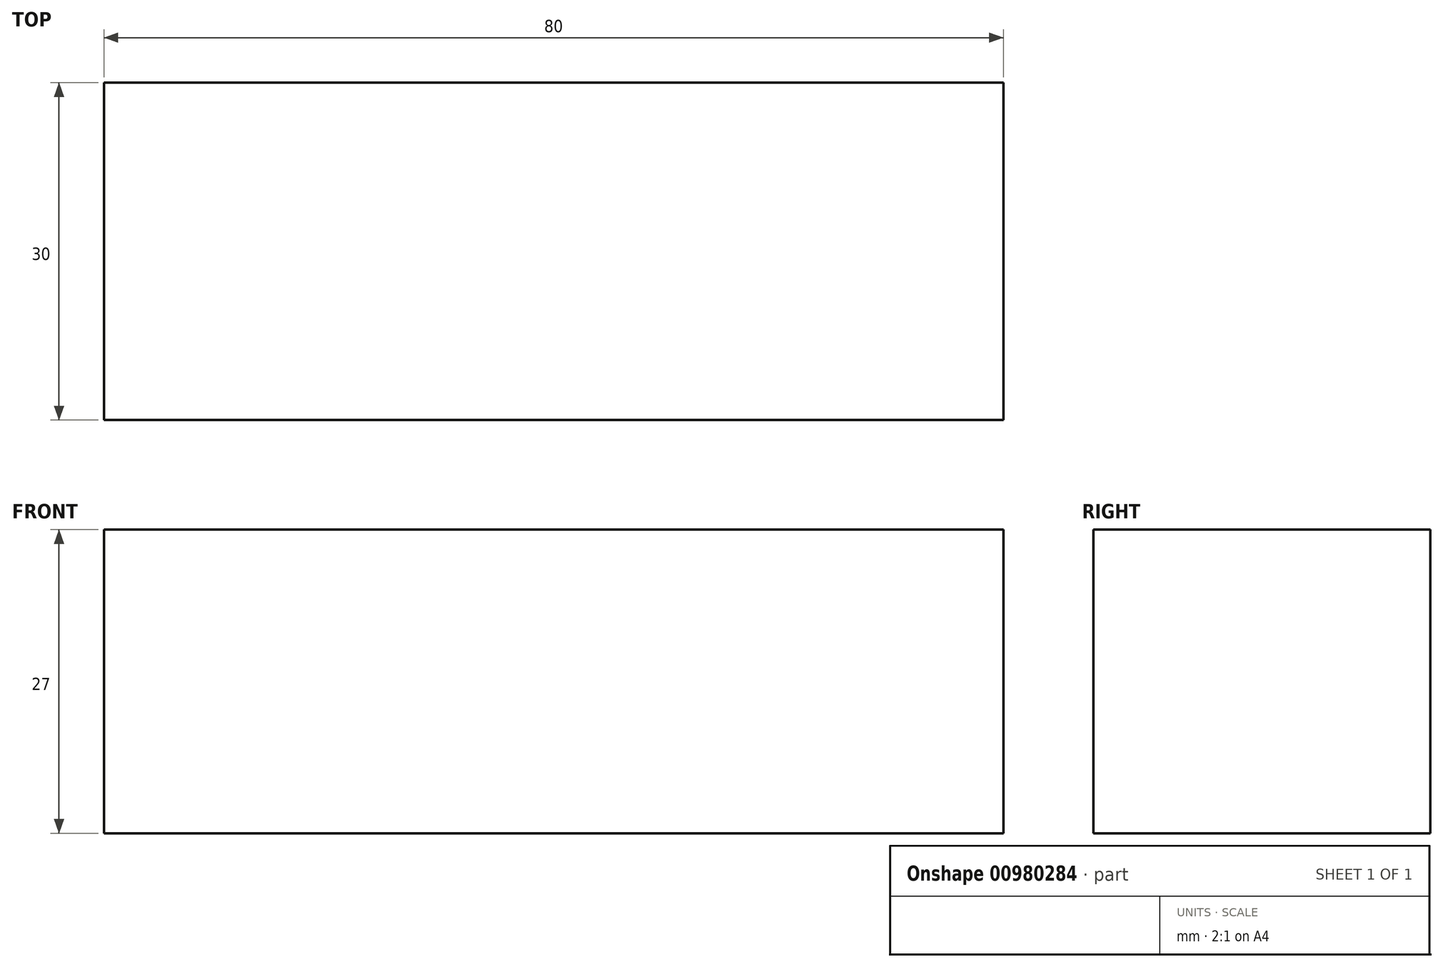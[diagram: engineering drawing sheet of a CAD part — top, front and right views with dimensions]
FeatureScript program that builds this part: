
annotation { "Feature Type Name" : "Feature", "Feature Type Description" : "" }
export const myFeature = defineFeature(function(context is Context, id is Id, definition is map)
    precondition{}
    {
        {
            assignVariable(context, id + "F0", {"name" : "Height", "anyValue" : 27});
        }
        {
            var Q0;
            Q0=qCreatedBy(makeId("Top.planeOp"),FACE);
            var sketch = newSketch(context, id + "F1", { "sketchPlane" : qUnion([Q0])});
            skLineSegment(sketch, "E0.bottom", {"start": v(40, 15) * mm, "end": v(-40, 15) * mm});
            skLineSegment(sketch, "E0.top", {"start": v(40, -15) * mm, "end": v(-40, -15) * mm});
            skLineSegment(sketch, "E0.left", {"start": v(40, 15) * mm, "end": v(40, -15) * mm});
            skLineSegment(sketch, "E0.right", {"start": v(-40, 15) * mm, "end": v(-40, -15) * mm});
            skPoint(sketch, "E0.middle", {"position": v(0, 0) * mm});
            skSolve(sketch);
        }
        {
            var Q0;
            Q0=makeQuery(id+"F1.imprint","IMPRINT",FACE,{"disambiguationData":[TD([[makeQuery(id+"F1.imprint","IMPRINT",EDGE,{"derivedFrom":sQuery(id+"F1.wireOp",EDGE,"E0.bottom")}),1.0]])]});
            extrude(context, id + "F2", {"entities" : qUnion([Q0]), "depth" : (getVariable(context, 'Height')) * mm, "offsetDistance" : 25 * mm});
        }
    });
